# Revit family: Pump_Commercial-Effluent-Zoeller-290_Non_Automatic Series
name_source: partatom
category: Mechanical Equipment
units: mm (PartAtom-declared; Revit-internal decimal feet)

## family parameters
Always vertical = No
Cut with Voids When Loaded = No
OmniClass Number = 23.60.30.21
OmniClass Title = Pumps
Part Type = Normal
Room Calculation Point = No
Round Connector Dimension = Use Radius
Shared = Yes
Work Plane-Based = Yes

## types (3) — shared parameters
Assembly Code = D2010900
Cooling = Oil Filled
Cord Length = 240"
Cord Type = UL listed, 3-wire neoprene cord and plug (1 Ph) or 4-wire cord and plug
Default Elevation = 0"
Description = Single Seal Non-Automatic Submersible Sewage or Dewatering Pumps
Discharge Diameter = 2" or 3" NPT
Discharge Height = 6"
Discharge Radius = 1"
Height = 19 5/16"
Hertz = 60
Impeller = Bronze
Impeller Type = Non-clogging vortex
Installation Type = Floor Mounted
Insulation = Class B
Lead Wires Insulation = Class B
Length = 12 7/8"
Manufacturer = Zoeller
Masterformat Number = 33 36 16
Masterformat Title = Utility Septic Tank Effluent Pumps
Material = Cast Iron-Zoeller-Powder Coated Epoxy
Max. Operating Temp. = 130.00 °F
Mechanical Seals = Carbon and Ceramic
Minimum Head = Not Applicable
Motor = 1/2 HP
Motor Protection = Auto reset thermal overload (1 Ph)
Motor Type = Submersible
Omniclass Table 23 Code = 23.60.30.21
Omniclass Table 23 Title = Pumps
Operation = Non-Automatic
Phase = 1 or 3 Ph
Price = Prices may vary. Please consult Manufacturer Representative for most up-to-date price list.
Product Page URL = https://zoellerpumps.com
RPM = 3450
Revised Date = 06/21/2024
Shipping Weight = 86-89 lbs
Solid Handling = 2" Spherical Solids
Square Ring & Gasket = Neoprene
Type = Permanent Split Capacitor or 3 Phase
Type Comments = Available in single or double seal designs.
URL = http://www.zoellerpumps.com
Warranty Information = 18 Months (Limited)
Waste Connection = Yes
Width = 8 1/4"

## per-type parameters (varying)
| type | Amps | Max. Flow at Min. Head | Maximum Head | Model | Voltage |
| 292 | 2.4-15.0 | 140 GPM @ 5' | 504" | 292 | 115-575 V |
| 294 | 3.8-17.8 | 196 GPM @ 5' | 744" | 294 | 200-575 V |
| 295 | 4.9-20.5 | 214 GPM @ 5' | 900" | 294 | 200-575 V |

## geometry (parser evidence)
native form markers: Sweep x3
no freeform markers — native parametric forms only
